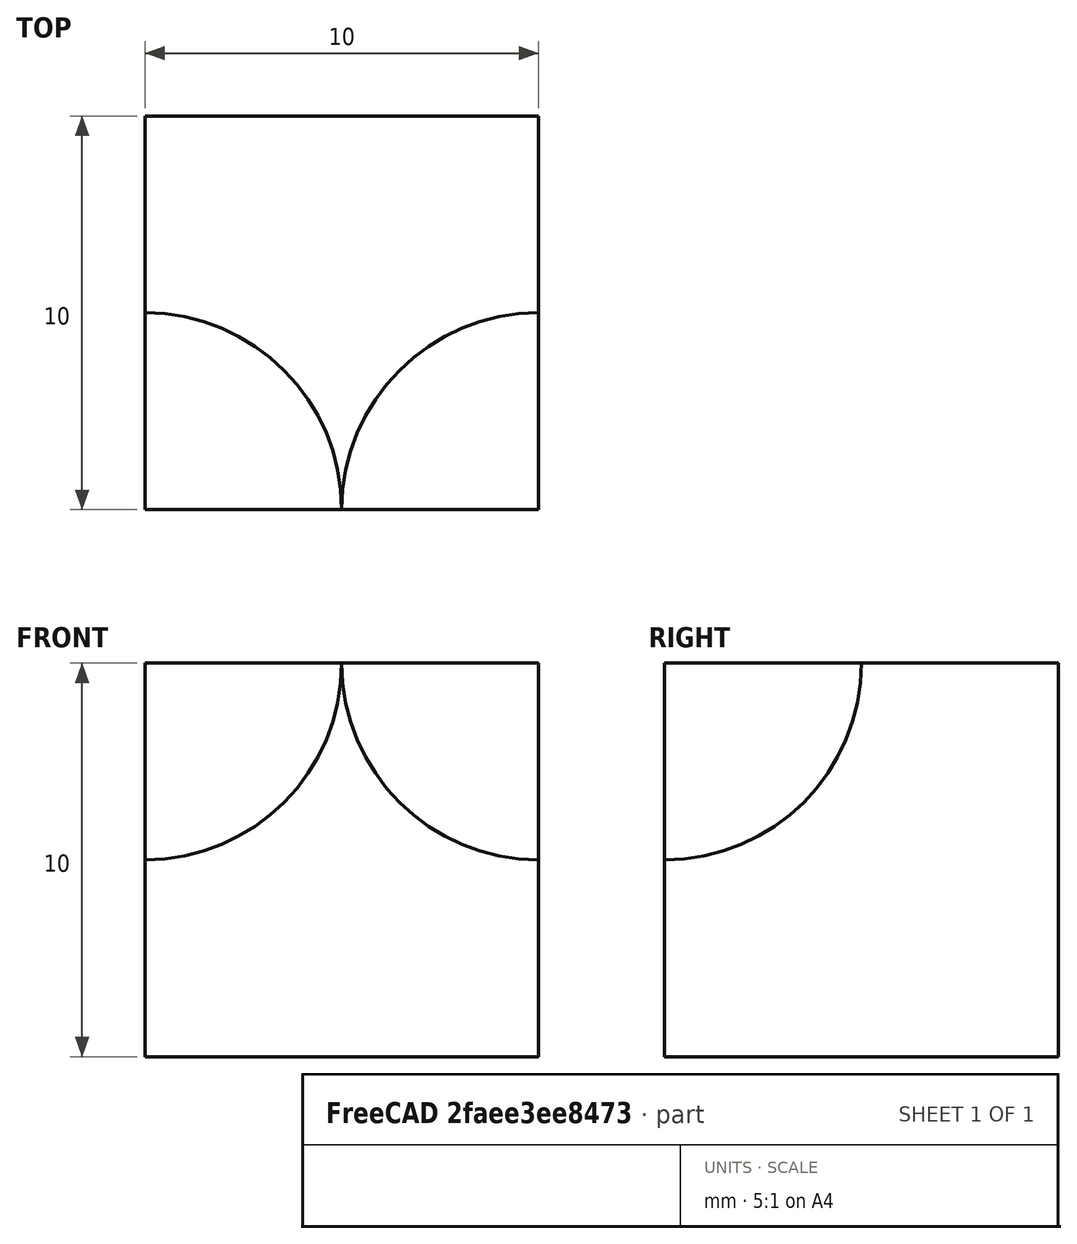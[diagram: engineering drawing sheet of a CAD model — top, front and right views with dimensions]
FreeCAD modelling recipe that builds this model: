
FCSTD DOCUMENT  (FreeCAD 0.16RUnknown)
Label: NeilsEg
License: All rights reserved
LicenseURL: http://en.wikipedia.org/wiki/All_rights_reserved
objects: Part::Cut×2, Part::Box×1, Part::Sphere×1, Part::FeaturePython×1, Spreadsheet::Sheet×1
note: 5 computed .brp shape members not serialized (recipe doc carries the construction recipe); baked Part::Feature solids carry a one-line shape summary decoded from their .brp

FEATURE [Part::Box] Box  label="Cube"
  Height = 10
  Length = 10
  Width = 10
FEATURE [Part::Sphere] Sphere
  Angle1 = -90
  Angle2 = 90
  Angle3 = 360
  Placement = pos=(0,0,10) rot=(0,0,1;0rad)
  Radius = 5
  expr: Radius = Spreadsheet.r
FEATURE [Part::Cut] Cut
  Base = -> Box
  Tool = -> Sphere
FEATURE [Part::FeaturePython] Clone  label="Clone of Sphere"  # Draft clone (typed FeaturePython)
  Objects = -> [Sphere]
  Placement = pos=(10,0,10) rot=(0,0,1;0rad)
  Scale = (1,1,1)
FEATURE [Part::Cut] Cut001
  Base = -> Cut
  Tool = -> Clone
FEATURE [Spreadsheet::Sheet] Spreadsheet
  cells = A1=radius; B1(r)==5 * 1
